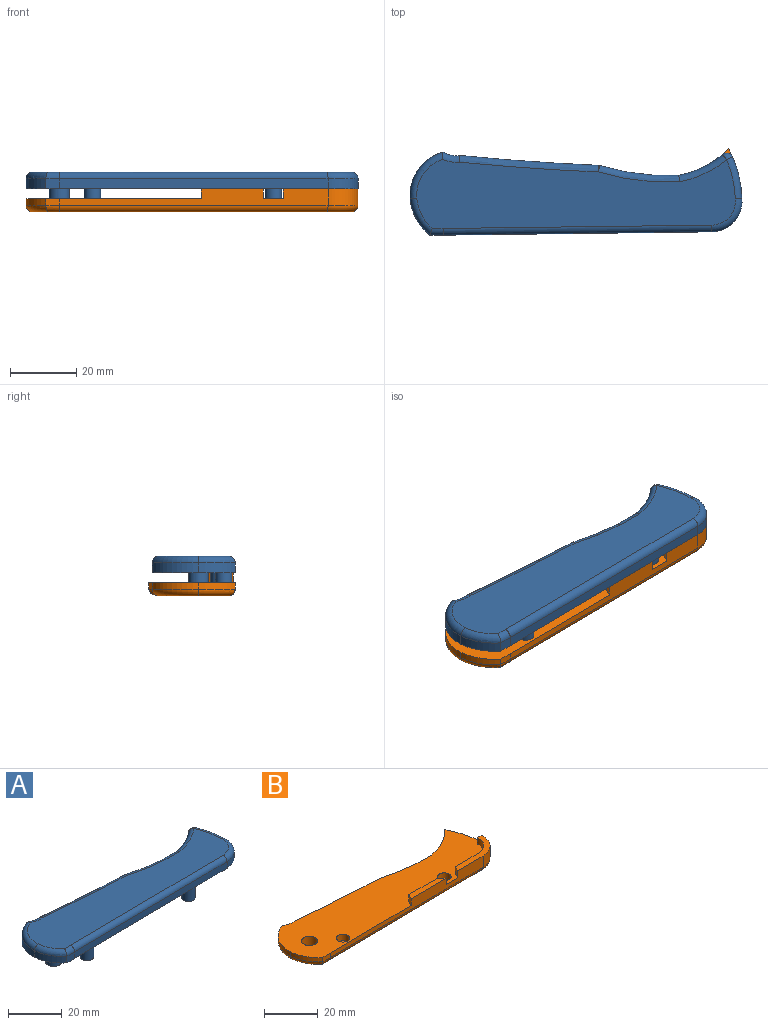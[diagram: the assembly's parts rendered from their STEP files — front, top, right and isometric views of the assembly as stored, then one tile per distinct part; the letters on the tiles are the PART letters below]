
ASSEMBLY  parts=2 mates=1
PART A: 32 faces, bbox 102.1x27.1x12 mm
  f0: cylinder r=750.23mm len=41.75mm, axis (0,0,-1), area 125.6mm2, adj f1,f11,f18,f31
  f1: cylinder r=7.84mm len=5.07mm, axis (0,0,-1), area 15.8mm2, adj f0,f2,f11,f19
  f2: cylinder r=13.61mm len=14mm, axis (0,0,-1), area 55.7mm2, adj f1,f3,f11,f20
  f3: cylinder r=15.94mm len=11mm, axis (0,0,-1), area 38.6mm2, adj f2,f4,f11,f21
  f4: plane 4x3mm, normal (0,-1,0), area 12mm2, adj f3,f5,f11,f22
  f5: plane 80.98x3mm, normal (0.01,-1,0), area 243mm2, adj f4,f6,f11,f23
  f6: cylinder r=9.15mm len=10mm, axis (0,0,-1), area 45.3mm2, adj f5,f7,f11,f24
  f7: cylinder r=33.68mm len=12.52mm, axis (0,0,-1), area 38.7mm2, adj f6,f11,f25,f26
  f8: cylinder r=29.12mm len=13.09mm, axis (0,0,-1), area 44mm2, adj f9,f11,f26,f28
  f9: cylinder r=71.79mm len=23.76mm, axis (0,0,-1), area 72.2mm2, adj f8,f11,f29,f31
  f10: plane 96.05x20.84mm, normal (0,0,1), area 1576.6mm2, adj f18,f19,f20,f21,f22,f23,f24,f25
  f11: plane 100.05x25mm, normal (0,0,-1), area 1965.3mm2, adj f0,f1,f2,f3,f4,f5,f6,f7
  f12: plane 5x5mm, normal (0,0,-1), area 19.6mm2, adj f13
  f13: cylinder r=2.5mm len=6mm, axis (0,0,1), area 94.2mm2, adj f11,f12
  f14: plane 5x5mm, normal (0,0,-1), area 19.6mm2, adj f15
  f15: cylinder r=2.5mm len=7mm, axis (0,0,1), area 110mm2, adj f11,f14
  f16: plane 6x6mm, normal (0,0,-1), area 28.3mm2, adj f17
  f17: cylinder r=3mm len=7mm, axis (0,0,1), area 131.9mm2, adj f11,f16
  f18: torus R=752.23mm, axis (0,0,1), area 131.4mm2, adj f0,f10,f19,f30
  f19: torus R=9.84mm, axis (0,0,1), area 16.8mm2, adj f1,f10,f18,f20
  f20: torus R=11.61mm, axis (0,0,1), area 54.2mm2, adj f2,f10,f19,f21
  f21: torus R=13.94mm, axis (0,0,1), area 37.8mm2, adj f3,f10,f20,f22
  f22: cylinder r=2mm len=4mm, axis (-1,0,0), area 11.7mm2, adj f4,f10,f21,f23
  f23: cylinder r=2mm len=81.01mm, axis (-1,-0.01,0), area 254.4mm2, adj f5,f10,f22,f24
  f24: torus R=7.15mm, axis (0,0,1), area 43.8mm2, adj f6,f10,f23,f25
  f25: torus R=31.68mm, axis (0,0,1), area 39.8mm2, adj f7,f10,f24,f27
  f26: cylinder r=2mm len=3.12mm, axis (0,0,1), area 11.1mm2, adj f7,f8,f11,f27
  f27: sphere r=2mm, area 7.4mm2, adj f25,f26,f28
  f28: torus R=31.12mm, axis (0,0,1), area 47.4mm2, adj f8,f10,f27,f29
  f29: torus R=73.79mm, axis (0,0,1), area 76.5mm2, adj f9,f10,f28,f30
  f30: sphere r=2mm, area 1mm2, adj f18,f29,f31
  f31: cylinder r=2mm len=3mm, axis (0,0,-1), area 1.5mm2, adj f0,f9,f11,f30
PART B: 35 faces, bbox 104.1x28.3x7 mm
  f0: cylinder r=2.5mm len=5mm, axis (0,0,-1), area 47.1mm2, adj f1,f24
  f1: plane 100.01x26mm, normal (0,0,1), area 1864.1mm2, adj f0,f2,f3,f4,f5,f6,f7,f9
  f2: cylinder r=750.23mm len=42mm, axis (0,0,-1), area 84.2mm2, adj f1,f3,f12,f29
  f3: cylinder r=7.84mm len=5.07mm, axis (0,0,-1), area 10.5mm2, adj f1,f2,f4,f27
  f4: cylinder r=13.61mm len=14mm, axis (0,0,-1), area 37.1mm2, adj f1,f3,f5,f25
  f5: cylinder r=15.94mm len=11mm, axis (0,0,-1), area 25.7mm2, adj f1,f4,f6,f26
  f6: plane 4x2mm, normal (0,-1,0), area 8mm2, adj f1,f5,f7,f28
  f7: plane 80.98x5mm, normal (0.01,-1,0), area 258.3mm2, adj f1,f6,f8,f15,f19,f21,f22,f23
  f8: cylinder r=9.15mm len=10mm, axis (0,0,-1), area 75.6mm2, adj f7,f9,f16,f19,f32
  f9: cylinder r=33.68mm len=15mm, axis (0,0,-1), area 31.3mm2, adj f1,f8,f10,f34
  f10: cylinder r=29.12mm len=15mm, axis (0,0,-1), area 34.5mm2, adj f1,f9,f12,f33
  f11: cylinder r=3mm len=6mm, axis (0,0,-1), area 75.4mm2, adj f1,f14
  f12: cylinder r=71.79mm len=24mm, axis (0,0,-1), area 48.6mm2, adj f1,f2,f10,f31
  f13: cylinder r=2.5mm len=5mm, axis (0,0,-1), area 62.8mm2, adj f1,f14,f30
  f14: plane 96.05x20.84mm, normal (0,0,-1), area 1529.7mm2, adj f11,f13,f25,f26,f27,f28,f29,f30
  f15: plane 3x2.69mm, normal (-0.88,0.48,0), area 9.2mm2, adj f1,f7,f18,f19
  f16: plane 3x2.04mm, normal (0,1,0), area 6.1mm2, adj f1,f8,f17,f19
  f17: cylinder r=6.98mm len=7.48mm, axis (0,0,-1), area 34.4mm2, adj f1,f16,f18,f19
  f18: plane 12.01x3mm, normal (0,1,0), area 36mm2, adj f1,f15,f17,f19
  f19: plane 22.52x10.17mm, normal (0,0,1), area 63.8mm2, adj f7,f8,f15,f16,f17,f18
  f20: plane 14.9x3mm, normal (0,1,0), area 44.7mm2, adj f1,f21,f22,f23
  f21: plane 3x2.44mm, normal (-0.89,0.45,0), area 8.2mm2, adj f1,f7,f20,f23
  f22: plane 3x2.49mm, normal (0.66,0.75,0), area 10mm2, adj f1,f7,f20,f23
  f23: plane 18.62x2.44mm, normal (0,0,1), area 39.1mm2, adj f7,f20,f21,f22
  f24: plane 5x5mm, normal (0,0,1), area 19.6mm2, adj f0
  f25: torus R=11.61mm, axis (0,0,1), area 54.2mm2, adj f4,f14,f26,f27
  f26: torus R=13.94mm, axis (0,0,1), area 37.8mm2, adj f5,f14,f25,f28
  f27: torus R=9.84mm, axis (0,0,1), area 16.7mm2, adj f3,f14,f25,f29
  f28: cylinder r=2mm len=4mm, axis (1,0,0), area 11.7mm2, adj f6,f14,f26,f30
  f29: torus R=752.23mm, axis (0,0,1), area 131.7mm2, adj f2,f14,f27,f31
  f30: cylinder r=2mm len=81.01mm, axis (1,0.01,0), area 253.4mm2, adj f7,f13,f14,f28,f32
  f31: torus R=73.79mm, axis (0,0,1), area 77mm2, adj f12,f14,f29,f33
  f32: torus R=7.15mm, axis (0,0,1), area 43.8mm2, adj f8,f14,f30,f34
  f33: torus R=31.12mm, axis (0,0,1), area 52.6mm2, adj f10,f14,f31,f34
  f34: torus R=31.68mm, axis (0,0,1), area 45.3mm2, adj f9,f14,f32,f33
PLACE A t=(3.95,-2.41,3.14)mm
PLACE B t=(50.37,-2.45,-3.86)mm
MATE fastened A.f13 <-> B.f0  axis (0,0,-1) through (-29.61,-9.99,-2.86)mm
